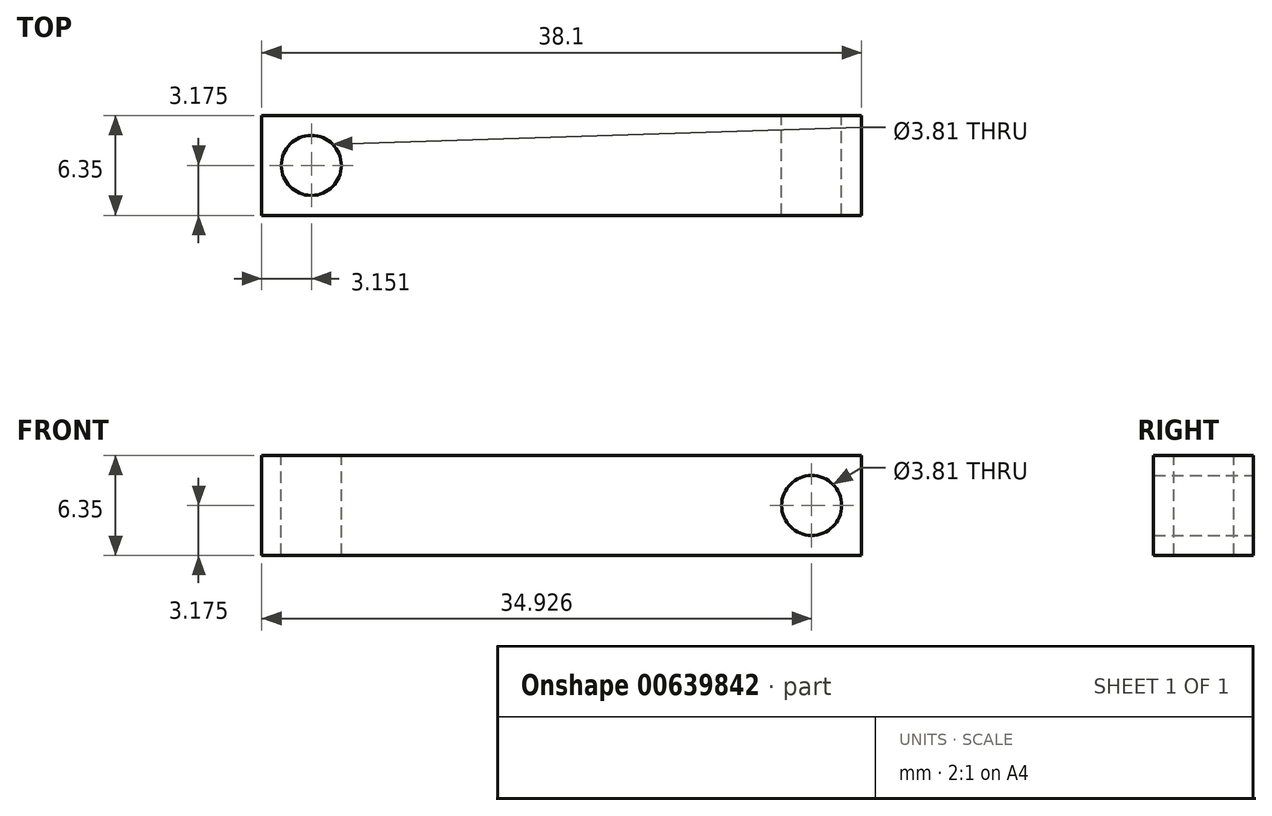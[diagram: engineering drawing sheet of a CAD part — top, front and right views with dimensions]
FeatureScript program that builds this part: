
annotation { "Feature Type Name" : "Feature", "Feature Type Description" : "" }
export const myFeature = defineFeature(function(context is Context, id is Id, definition is map)
    precondition{}
    {
        {
            var Q0;
            Q0=qCreatedBy(makeId("Front.planeOp"),FACE);
            var sketch = newSketch(context, id + "F0", { "sketchPlane" : qUnion([Q0])});
            skLineSegment(sketch, "E0.top", {"start": v(-37.28, -6.88) * mm, "end": v(0.82, -6.88) * mm});
            skLineSegment(sketch, "E0.left", {"start": v(-37.28, -0.53) * mm, "end": v(-37.28, -6.88) * mm});
            skLineSegment(sketch, "E0.right", {"start": v(0.82, -0.53) * mm, "end": v(0.82, -6.88) * mm});
            skPoint(sketch, "E1.center.orphan", {"position": v(32.1, 4.86) * mm});
            skPoint(sketch, "E2.center.orphan", {"position": v(33.27, 1.94) * mm});
            skLineSegment(sketch, "E3", {"start": v(-37.28, -0.53) * mm, "end": v(0.82, -0.53) * mm});
            skPoint(sketch, "E4.center.orphan", {"position": v(18.53, 1.94) * mm});
            skPoint(sketch, "E5.center.orphan", {"position": v(-28.35, 1.94) * mm});
            skPoint(sketch, "E6.centerSnap0", {"position": v(-37.28, -3.7) * mm});
            skCircle(sketch, "E7", {"center": v(-2.35, -3.7) * mm, "radius": 1.9 * mm});
            skSolve(sketch);
        }
        {
            var Q0;
            Q0 = qSketchRegion(id + "F0", true);
            var Q1;
            Q1=makeQuery(id+"F0.imprint","IMPRINT",FACE,{"disambiguationData":[TD([[makeQuery(id+"F0.imprint","IMPRINT",EDGE,{"derivedFrom":sQuery(id+"F0.wireOp",EDGE,"E6")}),1.0]])]});
            extrude(context, id + "F1", {"entities" : qUnion([Q0, Q1]), "depth" : 6.35 * mm, "offsetDistance" : 25.4 * mm});
        }
        {
            var Q0;
            Q0=makeQuery(id+"F1.opExtrude","SWEPT_FACE",FACE,{"disambiguationData":[OSD([sQuery(id+"F0.wireOp",EDGE,"E3")])]});
            var sketch = newSketch(context, id + "F2", { "sketchPlane" : qUnion([Q0])});
            skCircle(sketch, "E8", {"center": v(-34.13, -3.18) * mm, "radius": 1.9 * mm});
            skSolve(sketch);
        }
        {
            var Q0;
            Q0 = qSketchRegion(id + "F2", true);
            extrude(context, id + "F3", {"entities" : qUnion([Q0]), "operationType" : NewBodyOperationType.REMOVE, "oppositeDirection" : true, "depth" : 6.35 * mm, "offsetDistance" : 25.4 * mm});
        }
    });
